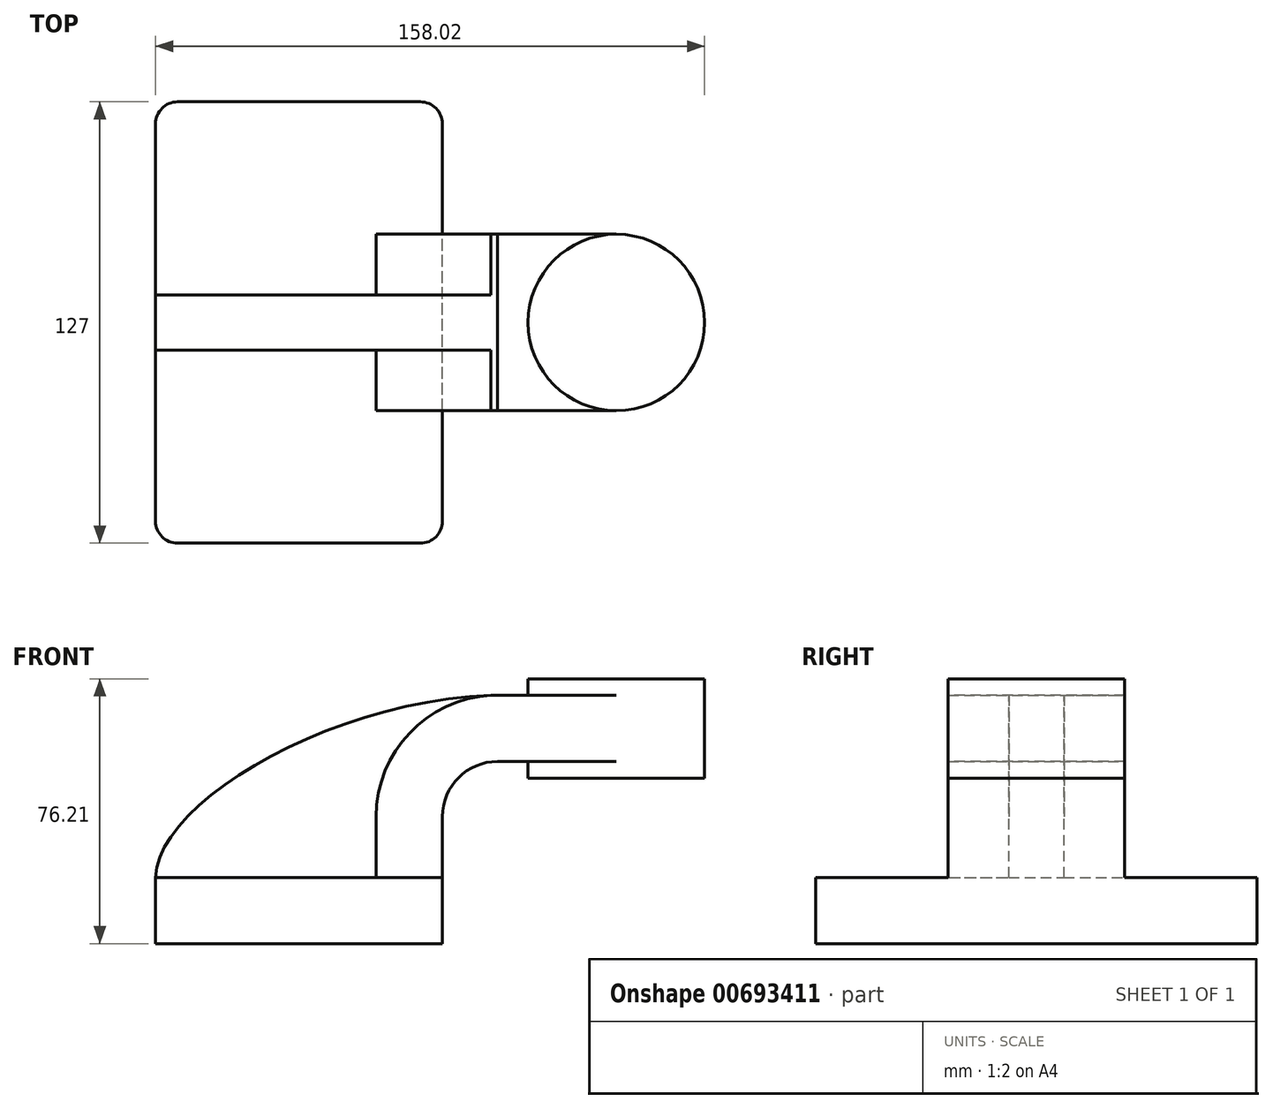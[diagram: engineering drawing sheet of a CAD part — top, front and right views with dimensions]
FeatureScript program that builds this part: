
annotation { "Feature Type Name" : "Feature", "Feature Type Description" : "" }
export const myFeature = defineFeature(function(context is Context, id is Id, definition is map)
    precondition{}
    {
        {
            var Q0;
            Q0=qCreatedBy(makeId("Front.planeOp"),FACE);
            var sketch = newSketch(context, id + "F0", { "sketchPlane" : qUnion([Q0])});
            skLineSegment(sketch, "E0.bottom", {"start": v(-41.28, -9.53) * mm, "end": v(41.28, -9.53) * mm});
            skLineSegment(sketch, "E0.top", {"start": v(-41.28, 9.53) * mm, "end": v(41.28, 9.53) * mm});
            skLineSegment(sketch, "E0.left", {"start": v(-41.28, -9.53) * mm, "end": v(-41.28, 9.53) * mm});
            skLineSegment(sketch, "E0.right", {"start": v(41.28, -9.53) * mm, "end": v(41.28, 9.53) * mm});
            skPoint(sketch, "E0.middle", {"position": v(0, 0) * mm});
            skLineSegment(sketch, "E1.bottom", {"start": v(65.94, 38.1) * mm, "end": v(116.74, 38.1) * mm});
            skLineSegment(sketch, "E1.top", {"start": v(65.94, 66.67) * mm, "end": v(116.74, 66.67) * mm});
            skLineSegment(sketch, "E1.left", {"start": v(65.94, 38.1) * mm, "end": v(65.94, 66.67) * mm});
            skLineSegment(sketch, "E1.right", {"start": v(116.74, 38.1) * mm, "end": v(116.74, 66.67) * mm});
            skPoint(sketch, "E1.middle", {"position": v(91.34, 52.39) * mm});
            skLineSegment(sketch, "E2", {"start": v(41.28, 9.53) * mm, "end": v(41.28, 27) * mm});
            skArc(sketch, "E3", {"start": v(41.27, 27) * mm, "mid": v(45.92, 38.23) * mm, "end": v(57.15, 42.88) * mm});
            skArc(sketch, "E4.1", {"start": v(22.22, 27) * mm, "mid": v(32.45, 51.7) * mm, "end": v(57.15, 61.93) * mm});
            skLineSegment(sketch, "E4.2", {"start": v(22.22, 9.53) * mm, "end": v(22.22, 27) * mm});
            skLineSegment(sketch, "E5", {"start": v(57.15, 42.88) * mm, "end": v(91.34, 42.88) * mm});
            skLineSegment(sketch, "E6", {"start": v(57.15, 61.93) * mm, "end": v(91.34, 61.93) * mm});
            skLineSegment(sketch, "E7", {"start": v(91.34, 66.67) * mm, "end": v(91.34, 38.1) * mm});
            skFitSpline(sketch, "E8", {"points": [v(-41.28, 9.53) * mm, v(57.15, 61.93) * mm], "startDerivative": vector(1.41, 64.94) * mm, "endDerivative": vector(142.46, 2.68) * mm});
            skSolve(sketch);
        }
        {
            var Q0;
            Q0=makeQuery(id+"F0.imprint","IMPRINT",FACE,{"disambiguationData":[TD([[makeQuery(id+"F0.imprint","IMPRINT",EDGE,{"derivedFrom":sQuery(id+"F0.wireOp",EDGE,"E0.bottom")}),1.0]])]});
            extrude(context, id + "F1", {"entities" : qUnion([Q0]), "endBound" : BoundingType.SYMMETRIC, "depth" : 127 * mm, "offsetDistance" : 25.4 * mm});
        }
        {
            var Q0;
            {var subQ1=sQuery(id+"F0.wireOp",EDGE,"E2");Q0=makeQuery(id+"F0.imprint","IMPRINT",FACE,{"disambiguationData":[TD([[makeQuery(id+"F0.imprint","IMPRINT",EDGE,{"derivedFrom":subQ1}),1.0]])]});}
            var Q1;
            {var subQ0=sQuery(id+"F0.wireOp",EDGE,"E5");var subQ1=sQuery(id+"F0.wireOp",EDGE,"E1.left");var subQ2=makeQuery(id+"F0.imprint","INTERSECT",VERTEX,{"derivedFrom":[subQ1,subQ0]});Q1=makeQuery(id+"F0.imprint","IMPRINT",FACE,{"disambiguationData":[TD([[makeQuery(id+"F0.imprint","IMPRINT",EDGE,{"disambiguationData":[TD([[subQ2,-1.0]])],"derivedFrom":subQ1}),-1.0]])]});}
            extrude(context, id + "F2", {"entities" : qUnion([Q0, Q1]), "operationType" : NewBodyOperationType.ADD, "endBound" : BoundingType.SYMMETRIC, "depth" : 50.8 * mm, "offsetDistance" : 25.4 * mm});
        }
        {
            var Q0;
            {var subQ3=sQuery(id+"F0.wireOp",EDGE,"E4.2");Q0=makeQuery(id+"F0.imprint","IMPRINT",FACE,{"disambiguationData":[TD([[makeQuery(id+"F0.imprint","IMPRINT",EDGE,{"derivedFrom":subQ3}),1.0]])]});}
            extrude(context, id + "F3", {"entities" : qUnion([Q0]), "operationType" : NewBodyOperationType.ADD, "endBound" : BoundingType.SYMMETRIC, "depth" : 15.88 * mm, "offsetDistance" : 25.4 * mm});
        }
        {
            var Q0;
            {var subQ4=sQuery(id+"F0.wireOp",EDGE,"E1.right");Q0=makeQuery(id+"F0.imprint","IMPRINT",FACE,{"disambiguationData":[TD([[makeQuery(id+"F0.imprint","IMPRINT",EDGE,{"derivedFrom":subQ4}),1.0]])]});}
            var Q1;
            Q1=sQuery(id+"F0.wireOp",EDGE,"E7");
            revolve(context, id + "F4", {"operationType" : NewBodyOperationType.ADD, "entities" : qUnion([Q0]), "axis" : qUnion([Q1]), "revolveType" : RevolveType.FULL});
        }
        {
            var Q0;
            Q0=makeQuery(id+"F1.opExtrude","CAP_EDGE",EDGE,{"disambiguationData":[OSD([sQuery(id+"F0.wireOp",EDGE,"E0.right")])],"isStart":false});
            var Q1;
            Q1=makeQuery(id+"F1.opExtrude","CAP_EDGE",EDGE,{"disambiguationData":[OSD([sQuery(id+"F0.wireOp",EDGE,"E0.left")])],"isStart":false});
            var Q2;
            Q2=makeQuery(id+"F1.opExtrude","CAP_EDGE",EDGE,{"disambiguationData":[OSD([sQuery(id+"F0.wireOp",EDGE,"E0.right")])],"isStart":true});
            var Q3;
            Q3=makeQuery(id+"F1.opExtrude","CAP_EDGE",EDGE,{"disambiguationData":[OSD([sQuery(id+"F0.wireOp",EDGE,"E0.left")])],"isStart":true});
            fillet(context, id + "F5", {"entities" : qUnion([Q0, Q1, Q2, Q3]), "radius" : 6.35 * mm, "tangentPropagation" : true, "allowEdgeOverflow" : false});
        }
    });
